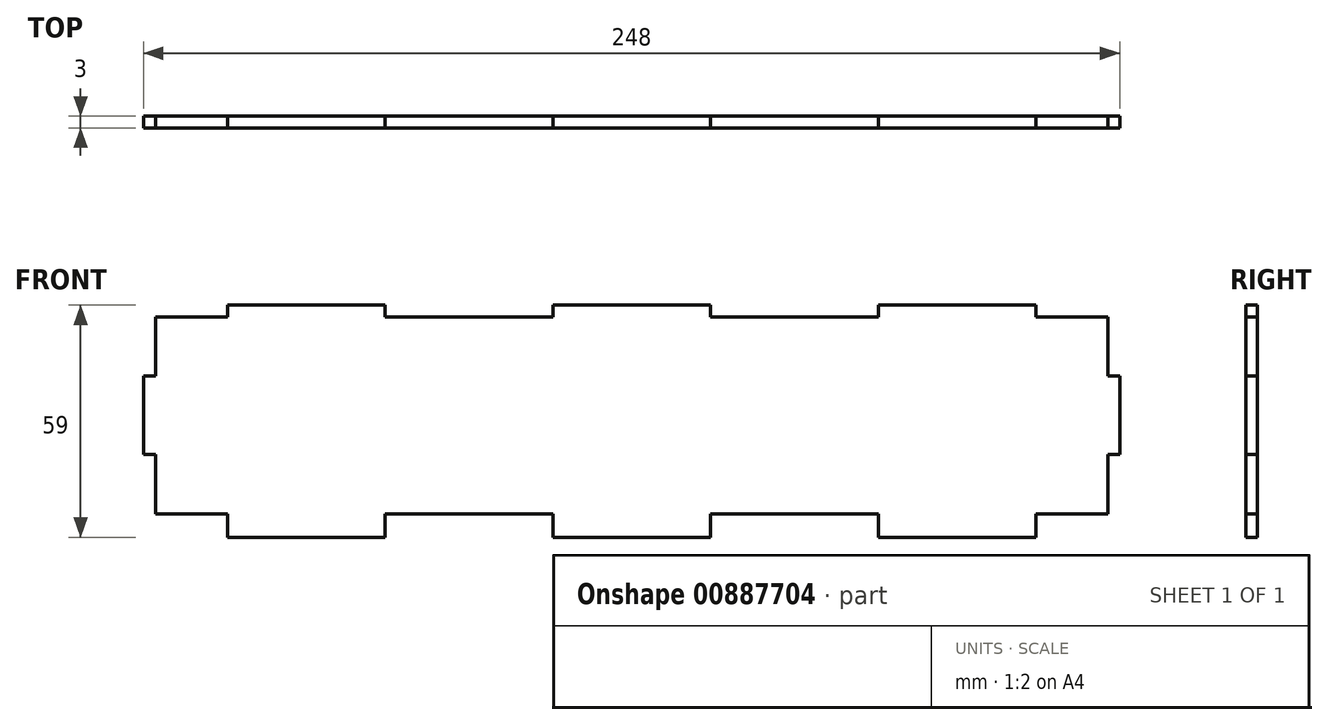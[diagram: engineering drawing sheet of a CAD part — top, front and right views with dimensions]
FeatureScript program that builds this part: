
annotation { "Feature Type Name" : "Feature", "Feature Type Description" : "" }
export const myFeature = defineFeature(function(context is Context, id is Id, definition is map)
    precondition{}
    {
        {
            var Q0;
            Q0=qCreatedBy(makeId("Front.planeOp"),FACE);
            var sketch = newSketch(context, id + "F0", { "sketchPlane" : qUnion([Q0])});
            skLineSegment(sketch, "E0.bottom", {"start": v(121, -25) * mm, "end": v(102.67, -25) * mm});
            skLineSegment(sketch, "E0.top", {"start": v(121, 25) * mm, "end": v(102.67, 25) * mm});
            skLineSegment(sketch, "E0.left", {"start": v(121, -25) * mm, "end": v(121, -10) * mm});
            skLineSegment(sketch, "E0.right", {"start": v(-121, -25) * mm, "end": v(-121, -10) * mm});
            skPoint(sketch, "E0.middle", {"position": v(0, 0) * mm});
            skLineSegment(sketch, "E1", {"start": v(-102.67, -25) * mm, "end": v(-102.67, -31) * mm});
            skLineSegment(sketch, "E2", {"start": v(-102.67, -31) * mm, "end": v(-62.67, -31) * mm});
            skLineSegment(sketch, "E3", {"start": v(-62.67, -31) * mm, "end": v(-62.67, -25) * mm});
            skLineSegment(sketch, "E4", {"start": v(-20, -25) * mm, "end": v(-20, -31) * mm});
            skLineSegment(sketch, "E5", {"start": v(-20, -31) * mm, "end": v(20, -31) * mm});
            skLineSegment(sketch, "E6", {"start": v(20, -31) * mm, "end": v(20, -25) * mm});
            skLineSegment(sketch, "E7.MirrorCS", {"start": v(62.67, -31) * mm, "end": v(62.67, -25) * mm});
            skLineSegment(sketch, "E8.MirrorCS", {"start": v(102.67, -31) * mm, "end": v(62.67, -31) * mm});
            skLineSegment(sketch, "E9.MirrorCS", {"start": v(102.67, -25) * mm, "end": v(102.67, -31) * mm});
            skLineSegment(sketch, "E10.trimOffspring", {"start": v(-102.67, -25) * mm, "end": v(-121, -25) * mm});
            skLineSegment(sketch, "E11.trimOffspring", {"start": v(-20, -25) * mm, "end": v(-62.67, -25) * mm});
            skLineSegment(sketch, "E12.trimOffspring", {"start": v(62.67, -25) * mm, "end": v(20, -25) * mm});
            skLineSegment(sketch, "E13", {"start": v(-102.67, 25) * mm, "end": v(-102.67, 28) * mm});
            skLineSegment(sketch, "E14", {"start": v(-102.67, 28) * mm, "end": v(-62.67, 28) * mm});
            skLineSegment(sketch, "E15", {"start": v(-62.67, 28) * mm, "end": v(-62.67, 25) * mm});
            skLineSegment(sketch, "E16", {"start": v(-20, 25) * mm, "end": v(-20, 28) * mm});
            skLineSegment(sketch, "E17", {"start": v(-20, 28) * mm, "end": v(20, 28) * mm});
            skLineSegment(sketch, "E18", {"start": v(20, 28) * mm, "end": v(20, 25) * mm});
            skLineSegment(sketch, "E19.trimOffspring", {"start": v(-102.67, 25) * mm, "end": v(-121, 25) * mm});
            skLineSegment(sketch, "E20.trimOffspring", {"start": v(-20, 25) * mm, "end": v(-62.67, 25) * mm});
            skLineSegment(sketch, "E21.MirrorCS", {"start": v(102.67, 28) * mm, "end": v(62.67, 28) * mm});
            skLineSegment(sketch, "E22.MirrorCS", {"start": v(62.67, 28) * mm, "end": v(62.67, 25) * mm});
            skLineSegment(sketch, "E23.MirrorCS", {"start": v(102.67, 25) * mm, "end": v(102.67, 28) * mm});
            skLineSegment(sketch, "E24", {"start": v(-121, 10) * mm, "end": v(-124, 10) * mm});
            skLineSegment(sketch, "E25", {"start": v(-124, 10) * mm, "end": v(-124, -10) * mm});
            skLineSegment(sketch, "E26", {"start": v(-124, -10) * mm, "end": v(-121, -10) * mm});
            skLineSegment(sketch, "E27.MirrorCS", {"start": v(124, 10) * mm, "end": v(124, -10) * mm});
            skLineSegment(sketch, "E28.MirrorCS", {"start": v(124, -10) * mm, "end": v(121, -10) * mm});
            skLineSegment(sketch, "E29.trimOffspring", {"start": v(-121, 10) * mm, "end": v(-121, 25) * mm});
            skLineSegment(sketch, "E30.MirrorCS", {"start": v(121, 10) * mm, "end": v(124, 10) * mm});
            skLineSegment(sketch, "E31.trimOffspring", {"start": v(121, 10) * mm, "end": v(121, 25) * mm});
            skLineSegment(sketch, "E32.trimOffspring", {"start": v(62.67, 25) * mm, "end": v(20, 25) * mm});
            skSolve(sketch);
        }
        {
            var Q0;
            Q0=makeQuery(id+"F0.imprint","IMPRINT",FACE,{"disambiguationData":[TD([[makeQuery(id+"F0.imprint","IMPRINT",EDGE,{"derivedFrom":sQuery(id+"F0.wireOp",EDGE,"E0.bottom")}),-1.0]])]});
            extrude(context, id + "F1", {"entities" : qUnion([Q0]), "depth" : 3 * mm, "offsetDistance" : 25 * mm});
        }
    });
